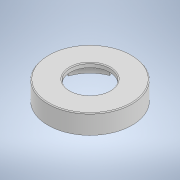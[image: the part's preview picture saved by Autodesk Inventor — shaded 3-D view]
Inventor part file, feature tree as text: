
AUTODESK INVENTOR PART (.ipt)
format: ipt  version: 2020 (Build 240168000, 168)  size: 297,984 bytes
history: native  units: mm
features: fillet x6, extrude x4, sketch x4
ambient origin geometry x8: Origin, YZ Plane, XZ Plane, XY Plane, X Axis, Y Axis, Z Axis, Center Point
bodies: Solid1 (feature_tree)
feature tree (14):
  extrude  "Extrusion1"  Depth=70.0mm
  extrude  "Extrusion2"  Depth=19.338248mm
  extrude  "Extrusion3"  Depth=4.0mm
  fillet  "Fillet1"  Radius=28.204521mm
  fillet  "Fillet2"  Radius=12.0mm
  fillet  "Fillet3"  Radius=33.0mm
  fillet  "Fillet4"  Radius=70.0mm
  fillet  "Fillet6"  Radius=4.0mm
  fillet  "Fillet7"  Radius=57.5mm
  extrude  "Extrusion4"  Depth=0.5mm
  sketch  "Sketch1"  dims[d0=57.5mm d1=70.0mm]
  sketch  "Sketch2"  dims[d2=68.0mm d4=19.338248mm]
  sketch  "Sketch3"  dims[d5=12.496557mm d7=3.211406mm d10=28.204521mm d11=12.0mm d12=0.0mm d13=33.0mm d14=70.0mm d15=4.0mm d16=0.0mm d18=57.5mm]
  sketch  "Sketch5"  dims[d19=68.0mm d20=2.0mm d21=2.0mm d22=0.122173mm d23=2.0mm d24=2.0mm d25=15.830136mm d26=2.0mm d27=2.0mm d28=31.293753mm d29=2.0mm d30=2.0mm d31=1.0mm d32=0.0mm d33=0.1mm d34=0.1mm d35=0.1mm d36=0.1mm d38=0.7mm d39=0.5mm d41=57.1mm d42=57.5mm d43=12.0mm d44=0.0mm d45=0.5mm d46=0.872665mm]
